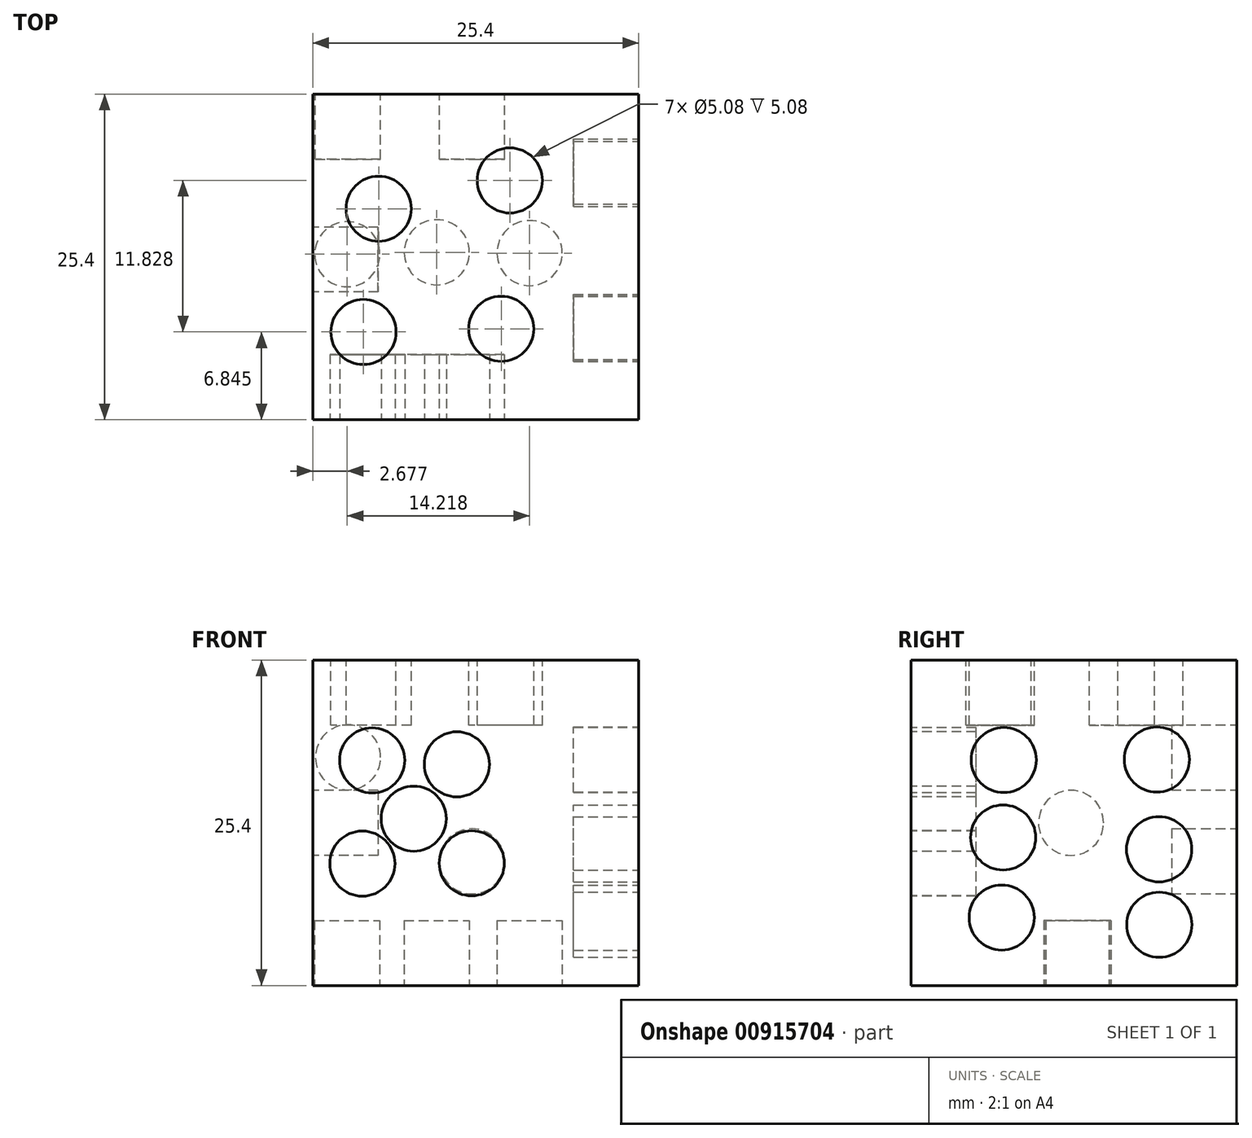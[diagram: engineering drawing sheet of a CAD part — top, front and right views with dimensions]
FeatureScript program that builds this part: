
annotation { "Feature Type Name" : "Feature", "Feature Type Description" : "" }
export const myFeature = defineFeature(function(context is Context, id is Id, definition is map)
    precondition{}
    {
        {
            var Q0;
            Q0=qCreatedBy(makeId("Top.planeOp"),FACE);
            var sketch = newSketch(context, id + "F0", { "sketchPlane" : qUnion([Q0])});
            skLineSegment(sketch, "E0.bottom", {"start": v(-153.97, -73.69) * mm, "end": v(-128.57, -73.69) * mm});
            skLineSegment(sketch, "E0.top", {"start": v(-153.97, -99.09) * mm, "end": v(-128.57, -99.09) * mm});
            skLineSegment(sketch, "E0.left", {"start": v(-153.97, -73.69) * mm, "end": v(-153.97, -99.09) * mm});
            skLineSegment(sketch, "E0.right", {"start": v(-128.57, -73.69) * mm, "end": v(-128.57, -99.09) * mm});
            skSolve(sketch);
        }
        {
            var Q0;
            Q0 = qSketchRegion(id + "F0", true);
            extrude(context, id + "F1", {"entities" : qUnion([Q0]), "depth" : 25.4 * mm, "offsetDistance" : 25.4 * mm});
        }
        {
            var Q0;
            Q0=makeQuery(id+"F1.opExtrude","SWEPT_FACE",FACE,{"disambiguationData":[OSD([sQuery(id+"F0.wireOp",EDGE,"E0.left")])]});
            var sketch = newSketch(context, id + "F2", { "sketchPlane" : qUnion([Q0])});
            skCircle(sketch, "E1", {"center": v(86.6, 12.69) * mm, "radius": 2.54 * mm});
            skSolve(sketch);
        }
        {
            var Q0;
            Q0 = qSketchRegion(id + "F2", true);
            extrude(context, id + "F3", {"entities" : qUnion([Q0]), "operationType" : NewBodyOperationType.REMOVE, "oppositeDirection" : true, "depth" : 5.08 * mm, "offsetDistance" : 25.4 * mm});
        }
        {
            var Q0;
            Q0=makeQuery(id+"F1.opExtrude","SWEPT_FACE",FACE,{"disambiguationData":[OSD([sQuery(id+"F0.wireOp",EDGE,"E0.right")])]});
            var sketch = newSketch(context, id + "F4", { "sketchPlane" : qUnion([Q0])});
            skCircle(sketch, "E2", {"center": v(-91.84, 17.6) * mm, "radius": 2.54 * mm});
            skSolve(sketch);
        }
        {
            var Q0;
            Q0=makeQuery(id+"F4.imprint","IMPRINT",FACE,{"disambiguationData":[TD([[makeQuery(id+"F4.imprint","IMPRINT",EDGE,{"derivedFrom":sQuery(id+"F4.wireOp",EDGE,"E2")}),1.0]])]});
            extrude(context, id + "F5", {"entities" : qUnion([Q0]), "operationType" : NewBodyOperationType.REMOVE, "oppositeDirection" : true, "depth" : 5.08 * mm, "offsetDistance" : 25.4 * mm});
        }
        {
            var Q0;
            Q0=makeQuery(id+"F1.opExtrude","SWEPT_FACE",FACE,{"disambiguationData":[OSD([sQuery(id+"F0.wireOp",EDGE,"E0.right")])]});
            var sketch = newSketch(context, id + "F6", { "sketchPlane" : qUnion([Q0])});
            skCircle(sketch, "E3", {"center": v(-79.9, 17.63) * mm, "radius": 2.54 * mm});
            skSolve(sketch);
        }
        {
            var Q0;
            Q0=makeQuery(id+"F6.imprint","IMPRINT",FACE,{"disambiguationData":[TD([[makeQuery(id+"F6.imprint","IMPRINT",EDGE,{"derivedFrom":sQuery(id+"F6.wireOp",EDGE,"E3")}),1.0]])]});
            extrude(context, id + "F7", {"entities" : qUnion([Q0]), "operationType" : NewBodyOperationType.REMOVE, "oppositeDirection" : true, "depth" : 5.08 * mm, "offsetDistance" : 25.4 * mm});
        }
        {
            var Q0;
            Q0=makeQuery(id+"F1.opExtrude","SWEPT_FACE",FACE,{"disambiguationData":[OSD([sQuery(id+"F0.wireOp",EDGE,"E0.right")])]});
            var sketch = newSketch(context, id + "F8", { "sketchPlane" : qUnion([Q0])});
            skCircle(sketch, "E4", {"center": v(-79.73, 10.63) * mm, "radius": 2.54 * mm});
            skSolve(sketch);
        }
        {
            var Q0;
            Q0 = qSketchRegion(id + "F8", true);
            extrude(context, id + "F9", {"entities" : qUnion([Q0]), "operationType" : NewBodyOperationType.REMOVE, "oppositeDirection" : true, "depth" : 5.08 * mm, "offsetDistance" : 25.4 * mm});
        }
        {
            var Q0;
            Q0=makeQuery(id+"F1.opExtrude","SWEPT_FACE",FACE,{"disambiguationData":[OSD([sQuery(id+"F0.wireOp",EDGE,"E0.right")])]});
            var sketch = newSketch(context, id + "F10", { "sketchPlane" : qUnion([Q0])});
            skCircle(sketch, "E5", {"center": v(-91.9, 11.55) * mm, "radius": 2.54 * mm});
            skSolve(sketch);
        }
        {
            var Q0;
            Q0=makeQuery(id+"F10.imprint","IMPRINT",FACE,{"disambiguationData":[TD([[makeQuery(id+"F10.imprint","IMPRINT",EDGE,{"derivedFrom":sQuery(id+"F10.wireOp",EDGE,"E5")}),1.0]])]});
            extrude(context, id + "F11", {"entities" : qUnion([Q0]), "operationType" : NewBodyOperationType.REMOVE, "oppositeDirection" : true, "depth" : 5.08 * mm, "offsetDistance" : 25.4 * mm});
        }
        {
            var Q0;
            Q0=makeQuery(id+"F1.opExtrude","SWEPT_FACE",FACE,{"disambiguationData":[OSD([sQuery(id+"F0.wireOp",EDGE,"E0.right")])]});
            var sketch = newSketch(context, id + "F12", { "sketchPlane" : qUnion([Q0])});
            skCircle(sketch, "E6", {"center": v(-92, 5.3) * mm, "radius": 2.54 * mm});
            skSolve(sketch);
        }
        {
            var Q0;
            Q0=makeQuery(id+"F12.imprint","IMPRINT",FACE,{"disambiguationData":[TD([[makeQuery(id+"F12.imprint","IMPRINT",EDGE,{"derivedFrom":sQuery(id+"F12.wireOp",EDGE,"E6")}),1.0]])]});
            extrude(context, id + "F13", {"entities" : qUnion([Q0]), "operationType" : NewBodyOperationType.REMOVE, "oppositeDirection" : true, "depth" : 5.08 * mm, "offsetDistance" : 25.4 * mm});
        }
        {
            var Q0;
            Q0=makeQuery(id+"F1.opExtrude","SWEPT_FACE",FACE,{"disambiguationData":[OSD([sQuery(id+"F0.wireOp",EDGE,"E0.right")])]});
            var sketch = newSketch(context, id + "F14", { "sketchPlane" : qUnion([Q0])});
            skCircle(sketch, "E7", {"center": v(-79.71, 4.74) * mm, "radius": 2.54 * mm});
            skSolve(sketch);
        }
        {
            var Q0;
            Q0 = qSketchRegion(id + "F14", true);
            extrude(context, id + "F15", {"entities" : qUnion([Q0]), "operationType" : NewBodyOperationType.REMOVE, "oppositeDirection" : true, "depth" : 5.08 * mm, "offsetDistance" : 25.4 * mm});
        }
        {
            var Q0;
            Q0=makeQuery(id+"F1.opExtrude","SWEPT_FACE",FACE,{"disambiguationData":[OSD([sQuery(id+"F0.wireOp",EDGE,"E0.bottom")])]});
            var sketch = newSketch(context, id + "F16", { "sketchPlane" : qUnion([Q0])});
            skCircle(sketch, "E8", {"center": v(141.56, 9.69) * mm, "radius": 2.54 * mm});
            skSolve(sketch);
        }
        {
            var Q0;
            Q0=makeQuery(id+"F16.imprint","IMPRINT",FACE,{"disambiguationData":[TD([[makeQuery(id+"F16.imprint","IMPRINT",EDGE,{"derivedFrom":sQuery(id+"F16.wireOp",EDGE,"E8")}),-1.0]])]});
            var sketch = newSketch(context, id + "F17", { "sketchPlane" : qUnion([Q0])});
            skCircle(sketch, "E9", {"center": v(151.23, 17.8) * mm, "radius": 2.54 * mm});
            skSolve(sketch);
        }
        {
            var Q0;
            Q0=makeQuery(id+"F16.imprint","IMPRINT",FACE,{"disambiguationData":[TD([[makeQuery(id+"F16.imprint","IMPRINT",EDGE,{"derivedFrom":sQuery(id+"F16.wireOp",EDGE,"E8")}),1.0]])]});
            extrude(context, id + "F18", {"entities" : qUnion([Q0]), "operationType" : NewBodyOperationType.REMOVE, "oppositeDirection" : true, "depth" : 5.08 * mm, "offsetDistance" : 25.4 * mm});
        }
        {
            var Q0;
            Q0=makeQuery(id+"F17.imprint","IMPRINT",FACE,{"disambiguationData":[TD([[makeQuery(id+"F17.imprint","IMPRINT",EDGE,{"derivedFrom":sQuery(id+"F17.wireOp",EDGE,"E9")}),1.0]])]});
            extrude(context, id + "F19", {"entities" : qUnion([Q0]), "operationType" : NewBodyOperationType.REMOVE, "oppositeDirection" : true, "depth" : 5.08 * mm, "offsetDistance" : 25.4 * mm});
        }
        {
            var Q0;
            Q0=makeQuery(id+"F1.opExtrude","CAP_FACE",FACE,{"disambiguationData":[OSD([sQuery(id+"F0.wireOp",EDGE,"E0.bottom"),sQuery(id+"F0.wireOp",EDGE,"E0.top"),sQuery(id+"F0.wireOp",EDGE,"E0.left"),sQuery(id+"F0.wireOp",EDGE,"E0.right")])],"isStart":false});
            var sketch = newSketch(context, id + "F20", { "sketchPlane" : qUnion([Q0])});
            skCircle(sketch, "E10", {"center": v(-139.29, -92) * mm, "radius": 2.54 * mm});
            skSolve(sketch);
        }
        {
            var Q0;
            Q0=makeQuery(id+"F20.imprint","IMPRINT",FACE,{"disambiguationData":[TD([[makeQuery(id+"F20.imprint","IMPRINT",EDGE,{"derivedFrom":sQuery(id+"F20.wireOp",EDGE,"E10")}),-1.0]])]});
            var sketch = newSketch(context, id + "F21", { "sketchPlane" : qUnion([Q0])});
            skCircle(sketch, "E11", {"center": v(-148.84, -82.63) * mm, "radius": 2.54 * mm});
            skSolve(sketch);
        }
        {
            var Q0;
            Q0=makeQuery(id+"F21.imprint","IMPRINT",FACE,{"disambiguationData":[TD([[makeQuery(id+"F21.imprint","IMPRINT",EDGE,{"derivedFrom":sQuery(id+"F21.wireOp",EDGE,"E11")}),-1.0]])]});
            var sketch = newSketch(context, id + "F22", { "sketchPlane" : qUnion([Q0])});
            skCircle(sketch, "E12", {"center": v(-138.61, -80.42) * mm, "radius": 2.54 * mm});
            skSolve(sketch);
        }
        {
            var Q0;
            Q0=makeQuery(id+"F20.imprint","IMPRINT",FACE,{"disambiguationData":[TD([[makeQuery(id+"F20.imprint","IMPRINT",EDGE,{"derivedFrom":sQuery(id+"F20.wireOp",EDGE,"E10")}),-1.0]])]});
            var sketch = newSketch(context, id + "F23", { "sketchPlane" : qUnion([Q0])});
            skCircle(sketch, "E13", {"center": v(-150.03, -92.25) * mm, "radius": 2.54 * mm});
            skSolve(sketch);
        }
        {
            var Q0;
            Q0=makeQuery(id+"F20.imprint","IMPRINT",FACE,{"disambiguationData":[TD([[makeQuery(id+"F20.imprint","IMPRINT",EDGE,{"derivedFrom":sQuery(id+"F20.wireOp",EDGE,"E10")}),1.0]])]});
            extrude(context, id + "F24", {"entities" : qUnion([Q0]), "operationType" : NewBodyOperationType.REMOVE, "oppositeDirection" : true, "depth" : 5.08 * mm, "offsetDistance" : 25.4 * mm});
        }
        {
            var Q0;
            Q0=makeQuery(id+"F23.imprint","IMPRINT",FACE,{"disambiguationData":[TD([[makeQuery(id+"F23.imprint","IMPRINT",EDGE,{"derivedFrom":sQuery(id+"F23.wireOp",EDGE,"E13")}),1.0]])]});
            extrude(context, id + "F25", {"entities" : qUnion([Q0]), "operationType" : NewBodyOperationType.REMOVE, "oppositeDirection" : true, "depth" : 5.08 * mm, "offsetDistance" : 25.4 * mm});
        }
        {
            var Q0;
            Q0=makeQuery(id+"F22.imprint","IMPRINT",FACE,{"disambiguationData":[TD([[makeQuery(id+"F22.imprint","IMPRINT",EDGE,{"derivedFrom":sQuery(id+"F22.wireOp",EDGE,"E12")}),1.0]])]});
            extrude(context, id + "F26", {"entities" : qUnion([Q0]), "operationType" : NewBodyOperationType.REMOVE, "oppositeDirection" : true, "depth" : 5.08 * mm, "offsetDistance" : 25.4 * mm});
        }
        {
            var Q0;
            Q0=makeQuery(id+"F21.imprint","IMPRINT",FACE,{"disambiguationData":[TD([[makeQuery(id+"F21.imprint","IMPRINT",EDGE,{"derivedFrom":sQuery(id+"F21.wireOp",EDGE,"E11")}),1.0]])]});
            extrude(context, id + "F27", {"entities" : qUnion([Q0]), "operationType" : NewBodyOperationType.REMOVE, "oppositeDirection" : true, "depth" : 5.08 * mm, "offsetDistance" : 25.4 * mm});
        }
        {
            var Q0;
            Q0=makeQuery(id+"F1.opExtrude","CAP_FACE",FACE,{"disambiguationData":[OSD([sQuery(id+"F0.wireOp",EDGE,"E0.bottom"),sQuery(id+"F0.wireOp",EDGE,"E0.top"),sQuery(id+"F0.wireOp",EDGE,"E0.left"),sQuery(id+"F0.wireOp",EDGE,"E0.right")])],"isStart":true});
            var sketch = newSketch(context, id + "F28", { "sketchPlane" : qUnion([Q0])});
            skCircle(sketch, "E14", {"center": v(-137.07, 86.09) * mm, "radius": 2.54 * mm});
            skSolve(sketch);
        }
        {
            var Q0;
            Q0=makeQuery(id+"F28.imprint","IMPRINT",FACE,{"disambiguationData":[TD([[makeQuery(id+"F28.imprint","IMPRINT",EDGE,{"derivedFrom":sQuery(id+"F28.wireOp",EDGE,"E14")}),1.0]])]});
            extrude(context, id + "F29", {"entities" : qUnion([Q0]), "operationType" : NewBodyOperationType.REMOVE, "oppositeDirection" : true, "depth" : 5.08 * mm, "offsetDistance" : 25.4 * mm});
        }
        {
            var Q0;
            Q0=makeQuery(id+"F1.opExtrude","CAP_FACE",FACE,{"disambiguationData":[OSD([sQuery(id+"F0.wireOp",EDGE,"E0.bottom"),sQuery(id+"F0.wireOp",EDGE,"E0.top"),sQuery(id+"F0.wireOp",EDGE,"E0.left"),sQuery(id+"F0.wireOp",EDGE,"E0.right")])],"isStart":true});
            var sketch = newSketch(context, id + "F30", { "sketchPlane" : qUnion([Q0])});
            skCircle(sketch, "E15", {"center": v(-144.31, 86.03) * mm, "radius": 2.54 * mm});
            skSolve(sketch);
        }
        {
            var Q0;
            Q0=makeQuery(id+"F30.imprint","IMPRINT",FACE,{"disambiguationData":[TD([[makeQuery(id+"F30.imprint","IMPRINT",EDGE,{"derivedFrom":sQuery(id+"F30.wireOp",EDGE,"E15")}),-1.0]])]});
            var sketch = newSketch(context, id + "F31", { "sketchPlane" : qUnion([Q0])});
            skCircle(sketch, "E16", {"center": v(-151.3, 86.18) * mm, "radius": 2.54 * mm});
            skSolve(sketch);
        }
        {
            var Q0;
            Q0=makeQuery(id+"F31.imprint","IMPRINT",FACE,{"disambiguationData":[TD([[makeQuery(id+"F31.imprint","IMPRINT",EDGE,{"derivedFrom":sQuery(id+"F31.wireOp",EDGE,"E16")}),1.0]])]});
            extrude(context, id + "F32", {"entities" : qUnion([Q0]), "operationType" : NewBodyOperationType.REMOVE, "oppositeDirection" : true, "depth" : 5.08 * mm, "offsetDistance" : 25.4 * mm});
        }
        {
            var Q0;
            Q0=makeQuery(id+"F30.imprint","IMPRINT",FACE,{"disambiguationData":[TD([[makeQuery(id+"F30.imprint","IMPRINT",EDGE,{"derivedFrom":sQuery(id+"F30.wireOp",EDGE,"E15")}),1.0]])]});
            extrude(context, id + "F33", {"entities" : qUnion([Q0]), "operationType" : NewBodyOperationType.REMOVE, "oppositeDirection" : true, "depth" : 5.08 * mm, "offsetDistance" : 25.4 * mm});
        }
        {
            var Q0;
            Q0=makeQuery(id+"F1.opExtrude","SWEPT_FACE",FACE,{"disambiguationData":[OSD([sQuery(id+"F0.wireOp",EDGE,"E0.top")])]});
            var sketch = newSketch(context, id + "F34", { "sketchPlane" : qUnion([Q0])});
            skCircle(sketch, "E17", {"center": v(-142.74, 17.26) * mm, "radius": 2.54 * mm});
            skSolve(sketch);
        }
        {
            var Q0;
            Q0=makeQuery(id+"F34.imprint","IMPRINT",FACE,{"disambiguationData":[TD([[makeQuery(id+"F34.imprint","IMPRINT",EDGE,{"derivedFrom":sQuery(id+"F34.wireOp",EDGE,"E17")}),1.0]])]});
            extrude(context, id + "F35", {"entities" : qUnion([Q0]), "operationType" : NewBodyOperationType.REMOVE, "oppositeDirection" : true, "depth" : 5.08 * mm, "offsetDistance" : 25.4 * mm});
        }
        {
            var Q0;
            Q0=makeQuery(id+"F1.opExtrude","SWEPT_FACE",FACE,{"disambiguationData":[OSD([sQuery(id+"F0.wireOp",EDGE,"E0.top")])]});
            var sketch = newSketch(context, id + "F36", { "sketchPlane" : qUnion([Q0])});
            skCircle(sketch, "E18", {"center": v(-146.1, 13.02) * mm, "radius": 2.54 * mm});
            skSolve(sketch);
        }
        {
            var Q0;
            Q0=makeQuery(id+"F36.imprint","IMPRINT",FACE,{"disambiguationData":[TD([[makeQuery(id+"F36.imprint","IMPRINT",EDGE,{"derivedFrom":sQuery(id+"F36.wireOp",EDGE,"E18")}),1.0]])]});
            extrude(context, id + "F37", {"entities" : qUnion([Q0]), "operationType" : NewBodyOperationType.REMOVE, "oppositeDirection" : true, "depth" : 5.08 * mm, "offsetDistance" : 25.4 * mm});
        }
        {
            var Q0;
            Q0=makeQuery(id+"F1.opExtrude","SWEPT_FACE",FACE,{"disambiguationData":[OSD([sQuery(id+"F0.wireOp",EDGE,"E0.top")])]});
            var sketch = newSketch(context, id + "F38", { "sketchPlane" : qUnion([Q0])});
            skCircle(sketch, "E19", {"center": v(-141.59, 9.54) * mm, "radius": 2.54 * mm});
            skSolve(sketch);
        }
        {
            var Q0;
            Q0=makeQuery(id+"F38.imprint","IMPRINT",FACE,{"disambiguationData":[TD([[makeQuery(id+"F38.imprint","IMPRINT",EDGE,{"derivedFrom":sQuery(id+"F38.wireOp",EDGE,"E19")}),1.0]])]});
            extrude(context, id + "F39", {"entities" : qUnion([Q0]), "operationType" : NewBodyOperationType.REMOVE, "oppositeDirection" : true, "depth" : 5.08 * mm, "offsetDistance" : 25.4 * mm});
        }
        {
            var Q0;
            Q0=makeQuery(id+"F1.opExtrude","SWEPT_FACE",FACE,{"disambiguationData":[OSD([sQuery(id+"F0.wireOp",EDGE,"E0.top")])]});
            var sketch = newSketch(context, id + "F40", { "sketchPlane" : qUnion([Q0])});
            skCircle(sketch, "E20", {"center": v(-149.35, 17.57) * mm, "radius": 2.54 * mm});
            skSolve(sketch);
        }
        {
            var Q0;
            Q0=makeQuery(id+"F40.imprint","IMPRINT",FACE,{"disambiguationData":[TD([[makeQuery(id+"F40.imprint","IMPRINT",EDGE,{"derivedFrom":sQuery(id+"F40.wireOp",EDGE,"E20")}),1.0]])]});
            extrude(context, id + "F41", {"entities" : qUnion([Q0]), "operationType" : NewBodyOperationType.REMOVE, "oppositeDirection" : true, "depth" : 5.08 * mm, "offsetDistance" : 25.4 * mm});
        }
        {
            var Q0;
            Q0=makeQuery(id+"F1.opExtrude","SWEPT_FACE",FACE,{"disambiguationData":[OSD([sQuery(id+"F0.wireOp",EDGE,"E0.top")])]});
            var sketch = newSketch(context, id + "F42", { "sketchPlane" : qUnion([Q0])});
            skCircle(sketch, "E21", {"center": v(-150.11, 9.5) * mm, "radius": 2.54 * mm});
            skSolve(sketch);
        }
        {
            var Q0;
            Q0=makeQuery(id+"F42.imprint","IMPRINT",FACE,{"disambiguationData":[TD([[makeQuery(id+"F42.imprint","IMPRINT",EDGE,{"derivedFrom":sQuery(id+"F42.wireOp",EDGE,"E21")}),1.0]])]});
            extrude(context, id + "F43", {"entities" : qUnion([Q0]), "operationType" : NewBodyOperationType.REMOVE, "oppositeDirection" : true, "depth" : 5.08 * mm, "offsetDistance" : 25.4 * mm});
        }
    });
